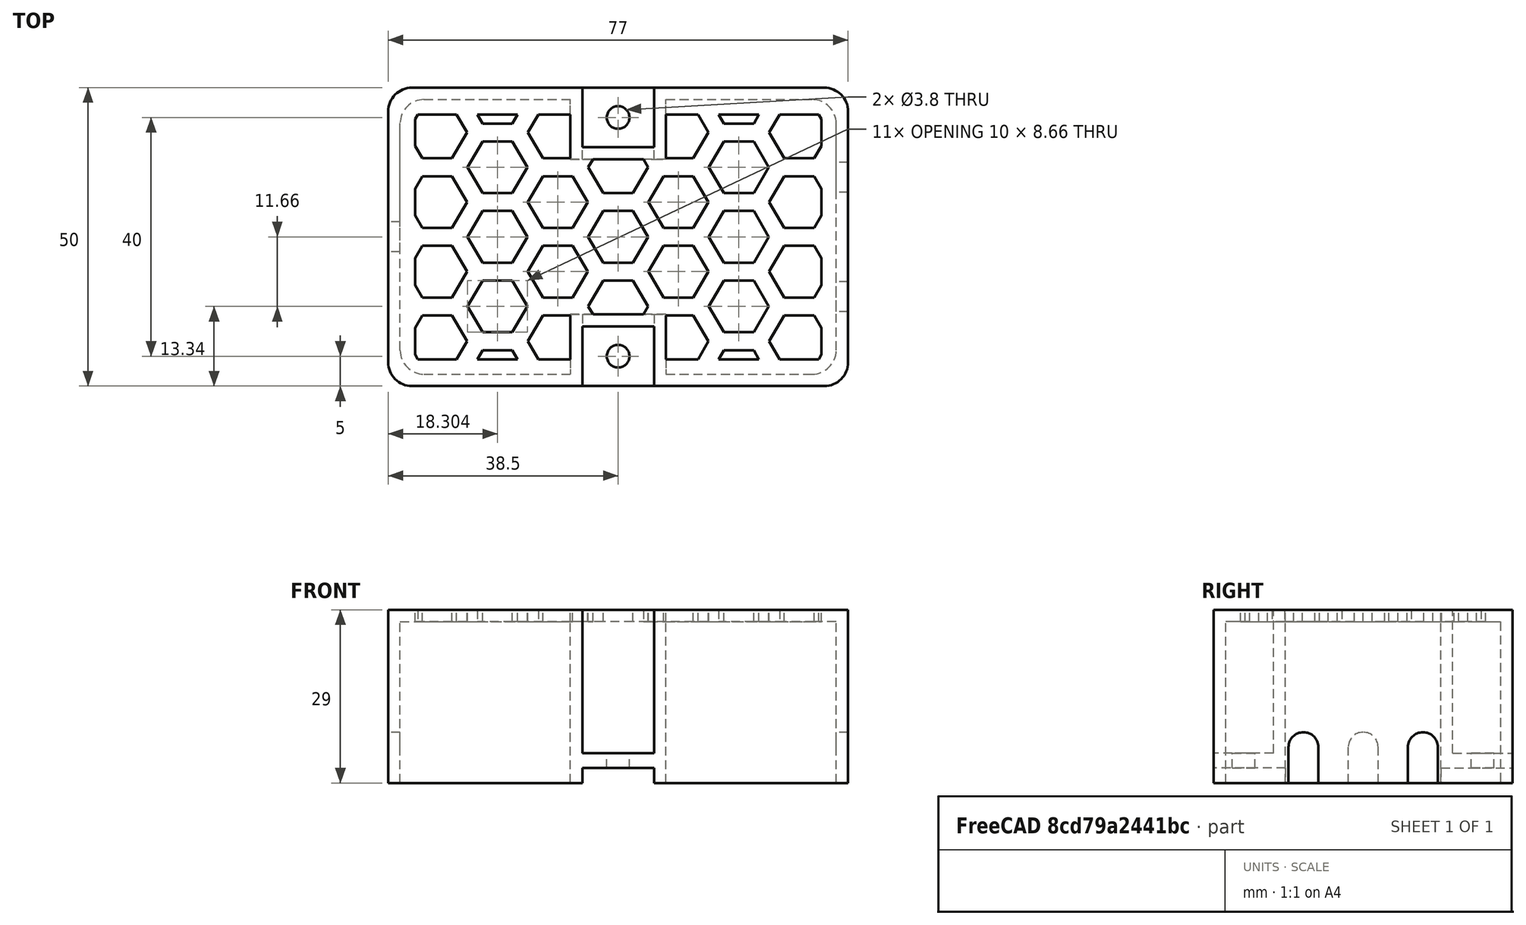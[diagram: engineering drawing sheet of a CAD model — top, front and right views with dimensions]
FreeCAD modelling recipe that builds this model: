
FCSTD DOCUMENT  (FreeCAD 0.19R)
Label: psu_cover
License: All rights reserved
LicenseURL: http://en.wikipedia.org/wiki/All_rights_reserved
objects: Part::Box×8, Part::MultiFuse×7, Part::Cut×4, Part::Mirroring×2, Part::Cylinder×2, Part::Fillet×2, PartDesign::FeatureBase×2, PartDesign::Body×2, Part::FeaturePython×1
note: 30 computed .brp shape members not serialized (recipe doc carries the construction recipe); baked Part::Feature solids carry a one-line shape summary decoded from their .brp

FEATURE [Part::Box] Box  label="external cube"
  AttacherType = Attacher::AttachEngine3D
  Height = 29
  Length = 77
  Placement = pos=(-38.5,-25,0) rot=(0,0,1;0rad)
  Width = 50
  expr: .Placement.Base.x = -Length / 2
  expr: .Placement.Base.y = -Width / 2
FEATURE [Part::Box] Box001  label="side cube"
  AttacherType = Attacher::AttachEngine3D
  Height = 29
  Length = 16
  Placement = pos=(-8,13,0) rot=(0,0,1;0rad)
  Width = 12
  expr: .Placement.Base.x = -Length / 2
  expr: .Placement.Base.y = <<external cube>>.Width / 2 - Width
  expr: Height = <<external cube>>.Height
  expr: Length = <<side extract cube>>.Length
FEATURE [Part::Box] Box002  label="bottom side center cube"
  AttacherType = Attacher::AttachEngine3D
  Height = 2.5
  Length = 12
  Placement = pos=(-6,0,0) rot=(0,0,1;0rad)
  Width = 25
  expr: .Placement.Base.x = -Length / 2
  expr: Length = <<side center cube>>.Length
  expr: Width = <<external cube>>.Width / 2
FEATURE [Part::Box] Box003  label="side center cube"
  AttacherType = Attacher::AttachEngine3D
  Height = 24
  Length = 12
  Placement = pos=(-6,15,5) rot=(0,0,1;0rad)
  Width = 10
  expr: Height = <<external cube>>.Height - .Placement.Base.z
  expr: .Placement.Base.y = <<external cube>>.Width / 2 - Width
  expr: .Placement.Base.x = -Length / 2
  expr: Width = <<side cube>>.Width - 2mm
  expr: Length = <<side cube>>.Length - 4mm
FEATURE [Part::Box] Box004  label="internal cube"
  AttacherType = Attacher::AttachEngine3D
  Height = 27
  Length = 73
  Placement = pos=(-36.5,-23,0) rot=(0,0,1;0rad)
  Width = 46
  expr: .Placement.Base.y = -Width / 2
  expr: .Placement.Base.x = -Length / 2
  expr: Width = <<external cube>>.Width - 4mm
  expr: Length = <<external cube>>.Length - 4mm
  expr: Height = <<external cube>>.Height - 2mm
FEATURE [Part::Box] Box005  label="side extract cube"
  AttacherType = Attacher::AttachEngine3D
  Height = 29
  Length = 16
  Placement = pos=(-8,13,0) rot=(0,0,1;0rad)
  Width = 12
  expr: Height = <<external cube>>.Height
  expr: .Placement.Base.y = <<external cube>>.Width / 2 - Width
  expr: .Placement.Base.x = -Length / 2
FEATURE [Part::Mirroring] Part__Mirroring  label="side extract cube (Mirror #1)"
  Base = (0,0,0)
  Normal = (0,1,0)
  Source = -> Box005
FEATURE [Part::MultiFuse] Fusion001  label="side extract fusion"
  Shapes = -> [Box005,Part__Mirroring]
FEATURE [Part::Cylinder] Cylinder  label="bolt hole"
  Angle = 360
  AttacherType = Attacher::AttachEngine3D
  Height = 29
  Placement = pos=(0,20,0) rot=(0,0,1;0rad)
  Radius = 1.9
  expr: Height = <<external cube>>.Height
FEATURE [Part::MultiFuse] Fusion  label="side cube extract"
  Shapes = -> [Box002,Box003,Cylinder]
FEATURE [Part::Cut] Cut001  label="side cut"
  Base = -> Box001
  Tool = -> Fusion
FEATURE [Part::Mirroring] Part__Mirroring001  label="side cut (Mirror #2)"
  Base = (0,0,0)
  Normal = (0,1,0)
  Source = -> Cut001
FEATURE [Part::Fillet] Fillet  label="external cube fillet"
  Base = -> Box
  Edges = 4 edges r=4: [Edge1,Edge3,Edge5,Edge7]
FEATURE [Part::Fillet] Fillet001  label="internal cube fillet"
  Base = -> Box004
  Edges = 4 edges r=4: [Edge1,Edge3,Edge5,Edge7]
FEATURE [Part::Cylinder] Cylinder001  label="wire hole"
  Angle = 360
  AttacherType = Attacher::AttachEngine3D
  Height = 10
  Placement = pos=(6,0,0) rot=(0,0,1;0rad)
  Radius = 2.5
FEATURE [Part::Box] Box006  label="wire hole cube"
  AttacherType = Attacher::AttachEngine3D
  Height = 10
  Length = 6
  Placement = pos=(0,-2.5,0) rot=(0,0,1;0rad)
  Width = 5
  expr: .Placement.Base.y = -Width / 2
  expr: Width = <<wire hole>>.Radius * 2
  expr: Length = <<wire hole>>.Placement.Base.x
FEATURE [Part::MultiFuse] Fusion003  label="wire hole fusion"
  Placement = pos=(-34,0,-8e-15) rot=(0,-1,0;1.5708rad)
  Shapes = -> [Cylinder001,Box006]
FEATURE [PartDesign::FeatureBase] Clone
  BaseFeature = -> Fusion003
  Placement = pos=(-34,0,-8e-15) rot=(0,-1,0;1.5708rad)
FEATURE [PartDesign::Body] Body  label="wire hole fusion clone"
  BaseFeature = -> Fusion003
  Group = -> [Clone]
  Origin = -> Origin
  Placement = pos=(77,-10,0) rot=(0,0,1;0rad)
  Tip = -> Clone
FEATURE [PartDesign::FeatureBase] Clone001
  BaseFeature = -> Fusion003
  Placement = pos=(-34,0,-8e-15) rot=(0,-1,0;1.5708rad)
FEATURE [PartDesign::Body] Body001  label="wire hole fusion clone001"
  BaseFeature = -> Fusion003
  Group = -> [Clone001]
  Origin = -> Origin001
  Placement = pos=(77,10,0) rot=(0,0,1;0rad)
  Tip = -> Clone001
FEATURE [Part::MultiFuse] Fusion004  label="wire hole fusion001"
  Shapes = -> [Fusion003,Body,Body001]
FEATURE [Part::FeaturePython] HoneycombSolid  # WARN: FeaturePython — macro-defined, semantics opaque (R4)
  Circumradius = 5
  Height = 2
  Length = 68
  Placement = pos=(-34,-20.5,27) rot=(0,0,1;0rad)
  Tickness = 3
  Width = 41
  expr: Length = <<internal cube>>.Length - 5mm
  expr: Width = <<internal cube>>.Width - 5mm
  expr: .Placement.Base.x = -Length / 2
  expr: .Placement.Base.y = -Width / 2
  expr: .Placement.Base.z = <<internal cube>>.Height
FEATURE [Part::Box] Box007  label="top wall"
  AttacherType = Attacher::AttachEngine3D
  Height = 2
  Length = 68
  Placement = pos=(-34,-20.5,27) rot=(0,0,1;0rad)
  Width = 41
  expr: Length = HoneycombSolid.Length
  expr: Width = HoneycombSolid.Width
  expr: Height = HoneycombSolid.Height
  expr: .Placement.Base.x = HoneycombSolid.Placement.Base.x
  expr: .Placement.Base.y = HoneycombSolid.Placement.Base.y
  expr: .Placement.Base.z = HoneycombSolid.Placement.Base.z
FEATURE [Part::MultiFuse] Fusion007  label="box extract fusion"
  Shapes = -> [Fillet001,Box007]
FEATURE [Part::Cut] Cut  label="box cut"
  Base = -> Fillet
  Tool = -> Fusion007
FEATURE [Part::MultiFuse] Fusion006  label="box fusion"
  Shapes = -> [HoneycombSolid,Cut]
FEATURE [Part::Cut] Cut003  label="box cut001"
  Base = -> Fusion006
  Tool = -> Fusion001
FEATURE [Part::MultiFuse] Fusion002  label="body fusion"
  Shapes = -> [Part__Mirroring001,Cut001,Cut003]
FEATURE [Part::Cut] Cut002  label="body cut"
  Base = -> Fusion002
  Tool = -> Fusion004
